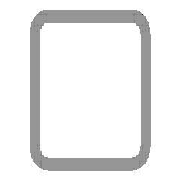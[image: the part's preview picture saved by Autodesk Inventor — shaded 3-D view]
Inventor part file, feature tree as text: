
AUTODESK INVENTOR PART (.ipt)
format: ipt  version: 2025.1 (Build 291241020, 241B)  size: 134,656 bytes
history: native  units: mm (DEFAULTED — no unit token found)
features: other x4, sketch x1, plane x1
ambient origin geometry x8: Origin, YZ Plane, XZ Plane, XY Plane, X Axis, Y Axis, Z Axis, Center Point
bodies: Solid1 (feature_tree), Body (feature_tree)
feature tree (6):
  parser-record x1  (decoder bookkeeping rows leaked as tree rows — omitted from the tree; the rows remain in map.json)
  other  "Driven Length"
  other  "Start plane"
  other  "End plane"
  sketch  "Sketch3"  dims[d3=790.0mm d4=0.0mm d7=6.0mm d9=100.0mm d11=100.0mm d12=3.0mm d13=100.0mm d14=890.0mm d15=50.0mm d16=50.0mm d17=90.0deg d18=790.0mm]
  plane  "Work Plane3"
